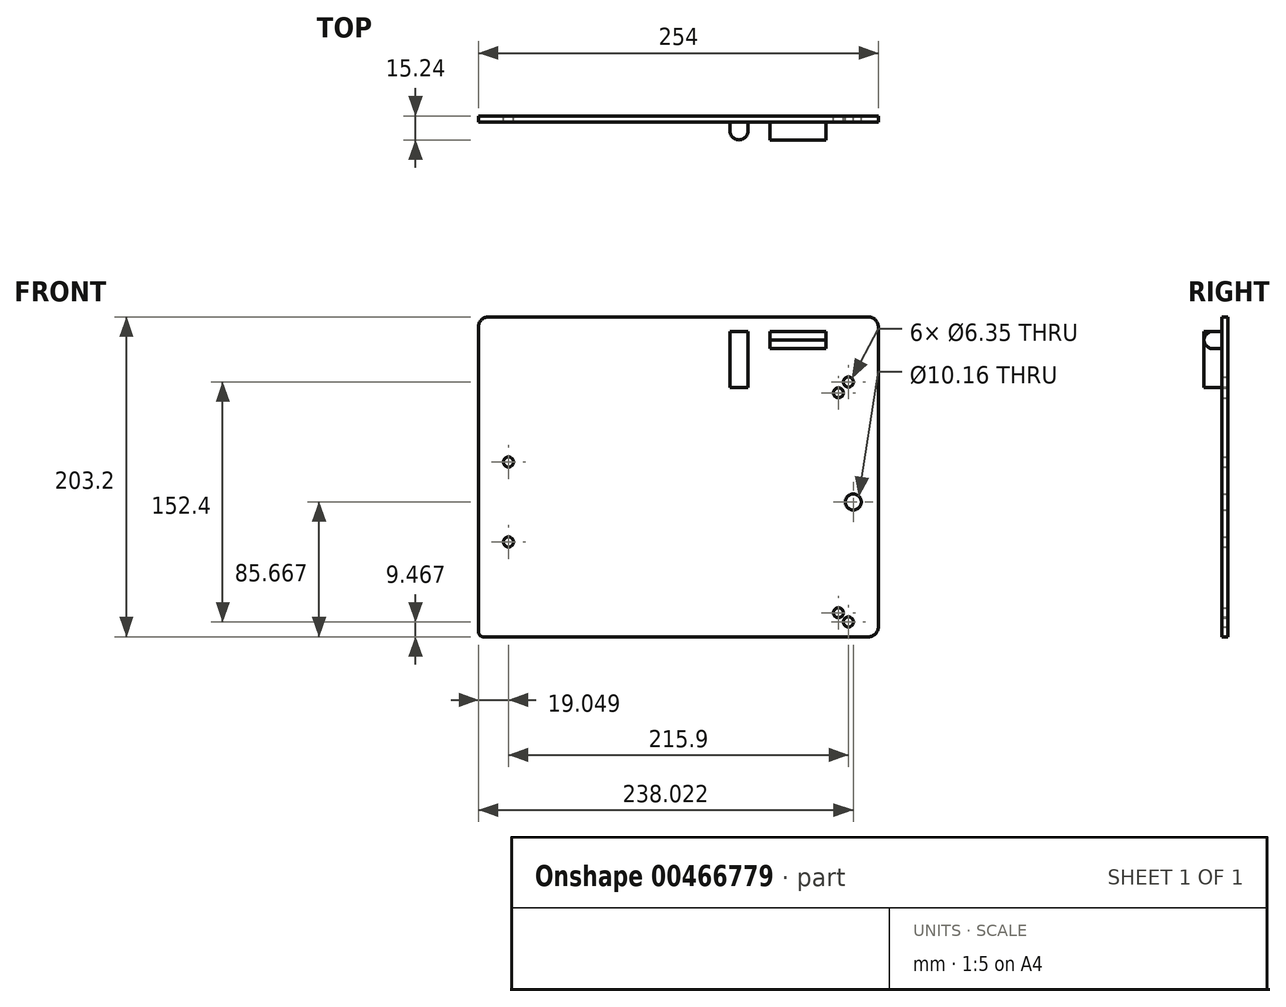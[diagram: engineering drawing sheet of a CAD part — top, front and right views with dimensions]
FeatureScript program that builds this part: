
annotation { "Feature Type Name" : "Feature", "Feature Type Description" : "" }
export const myFeature = defineFeature(function(context is Context, id is Id, definition is map)
    precondition{}
    {
        {
            var Q0;
            Q0=qCreatedBy(makeId("Front.planeOp"),FACE);
            var sketch = newSketch(context, id + "F0", { "sketchPlane" : qUnion([Q0])});
            skLineSegment(sketch, "E0.bottom", {"start": v(5.58, 3.84) * mm, "end": v(246.88, 3.84) * mm});
            skLineSegment(sketch, "E0.top", {"start": v(2.5, -199.36) * mm, "end": v(246.88, -199.36) * mm});
            skLineSegment(sketch, "E0.left", {"start": v(-0.77, -2.5) * mm, "end": v(-0.77, -196.08) * mm});
            skLineSegment(sketch, "E0.right", {"start": v(253.23, -2.5) * mm, "end": v(253.23, -193) * mm});
            skArc(sketch, "E1.filletArc", {"start": v(253.23, -2.5) * mm, "mid": v(251.37, 1.98) * mm, "end": v(246.88, 3.84) * mm});
            skArc(sketch, "E2.filletArc", {"start": v(5.58, 3.84) * mm, "mid": v(1.09, 1.98) * mm, "end": v(-0.77, -2.5) * mm});
            skArc(sketch, "E3.filletArc", {"start": v(-0.77, -196.08) * mm, "mid": v(0.19, -198.4) * mm, "end": v(2.5, -199.36) * mm});
            skArc(sketch, "E4.filletArc", {"start": v(246.88, -199.36) * mm, "mid": v(251.37, -197.5) * mm, "end": v(253.23, -193) * mm});
            skCircle(sketch, "E5", {"center": v(234.18, -189.9) * mm, "radius": 3.18 * mm});
            skCircle(sketch, "E6", {"center": v(234.18, -37.5) * mm, "radius": 3.18 * mm});
            skLineSegment(sketch, "E7", {"start": v(237.25, -113.7) * mm, "end": v(13.19, -113.7) * mm});
            skCircle(sketch, "E8", {"center": v(18.28, -139.1) * mm, "radius": 3.18 * mm});
            skCircle(sketch, "E9", {"center": v(18.28, -88.3) * mm, "radius": 3.18 * mm});
            skCircle(sketch, "E10", {"center": v(237.25, -113.7) * mm, "radius": 5.08 * mm});
            skCircle(sketch, "E11", {"center": v(227.83, -44.38) * mm, "radius": 3.18 * mm});
            skCircle(sketch, "E12", {"center": v(227.83, -184.08) * mm, "radius": 3.18 * mm});
            skLineSegment(sketch, "E13.bottom", {"start": v(184.35, -5.32) * mm, "end": v(219.91, -5.32) * mm});
            skLineSegment(sketch, "E13.top", {"start": v(184.35, -16.31) * mm, "end": v(219.91, -16.31) * mm});
            skLineSegment(sketch, "E13.left", {"start": v(184.35, -5.32) * mm, "end": v(184.35, -16.31) * mm});
            skLineSegment(sketch, "E13.right", {"start": v(219.91, -5.32) * mm, "end": v(219.91, -16.31) * mm});
            skLineSegment(sketch, "E14.bottom", {"start": v(170.38, -5.32) * mm, "end": v(158.95, -5.32) * mm});
            skLineSegment(sketch, "E14.top", {"start": v(170.38, -40.88) * mm, "end": v(158.95, -40.88) * mm});
            skLineSegment(sketch, "E14.left", {"start": v(170.38, -5.32) * mm, "end": v(170.38, -40.88) * mm});
            skLineSegment(sketch, "E14.right", {"start": v(158.95, -5.32) * mm, "end": v(158.95, -40.88) * mm});
            skSolve(sketch);
        }
        {
            var Q0;
            Q0=makeQuery(id+"F0.imprint","IMPRINT",FACE,{"disambiguationData":[TD([[makeQuery(id+"F0.imprint","IMPRINT",EDGE,{"derivedFrom":sQuery(id+"F0.wireOp",EDGE,"E0.bottom")}),-1.0]])]});
            var Q1;
            Q1=makeQuery(id+"F0.imprint","IMPRINT",FACE,{"disambiguationData":[TD([[makeQuery(id+"F0.imprint","IMPRINT",EDGE,{"derivedFrom":sQuery(id+"F0.wireOp",EDGE,"E14.bottom")}),1.0]])]});
            var Q2;
            Q2=makeQuery(id+"F0.imprint","IMPRINT",FACE,{"disambiguationData":[TD([[makeQuery(id+"F0.imprint","IMPRINT",EDGE,{"derivedFrom":sQuery(id+"F0.wireOp",EDGE,"E13.bottom")}),-1.0]])]});
            extrude(context, id + "F1", {"entities" : qUnion([Q0, Q1, Q2]), "depth" : 3.8 * mm});
        }
        {
            var Q0;
            Q0=makeQuery(id+"F0.imprint","IMPRINT",FACE,{"disambiguationData":[TD([[makeQuery(id+"F0.imprint","IMPRINT",EDGE,{"derivedFrom":sQuery(id+"F0.wireOp",EDGE,"E14.bottom")}),1.0]])]});
            var Q1;
            Q1=makeQuery(id+"F0.imprint","IMPRINT",FACE,{"disambiguationData":[TD([[makeQuery(id+"F0.imprint","IMPRINT",EDGE,{"derivedFrom":sQuery(id+"F0.wireOp",EDGE,"E13.bottom")}),-1.0]])]});
            extrude(context, id + "F2", {"entities" : qUnion([Q0, Q1]), "operationType" : NewBodyOperationType.ADD, "depth" : 15.24 * mm});
        }
        {
            var Q0;
            Q0=makeQuery(id+"F2.opExtrude","CAP_EDGE",EDGE,{"disambiguationData":[OSD([sQuery(id+"F0.wireOp",EDGE,"E14.right")])],"isStart":false});
            var Q1;
            Q1=makeQuery(id+"F2.opExtrude","CAP_EDGE",EDGE,{"disambiguationData":[OSD([sQuery(id+"F0.wireOp",EDGE,"E13.bottom")])],"isStart":false});
            var Q2;
            Q2=makeQuery(id+"F2.opExtrude","CAP_EDGE",EDGE,{"disambiguationData":[OSD([sQuery(id+"F0.wireOp",EDGE,"E13.top")])],"isStart":false});
            var Q3;
            Q3=makeQuery(id+"F2.opExtrude","CAP_EDGE",EDGE,{"disambiguationData":[OSD([sQuery(id+"F0.wireOp",EDGE,"E14.left")])],"isStart":false});
            fillet(context, id + "F3", {"entities" : qUnion([Q0, Q1, Q2, Q3]), "radius" : 5.6 * mm, "tangentPropagation" : true, "allowEdgeOverflow" : false});
        }
    });
